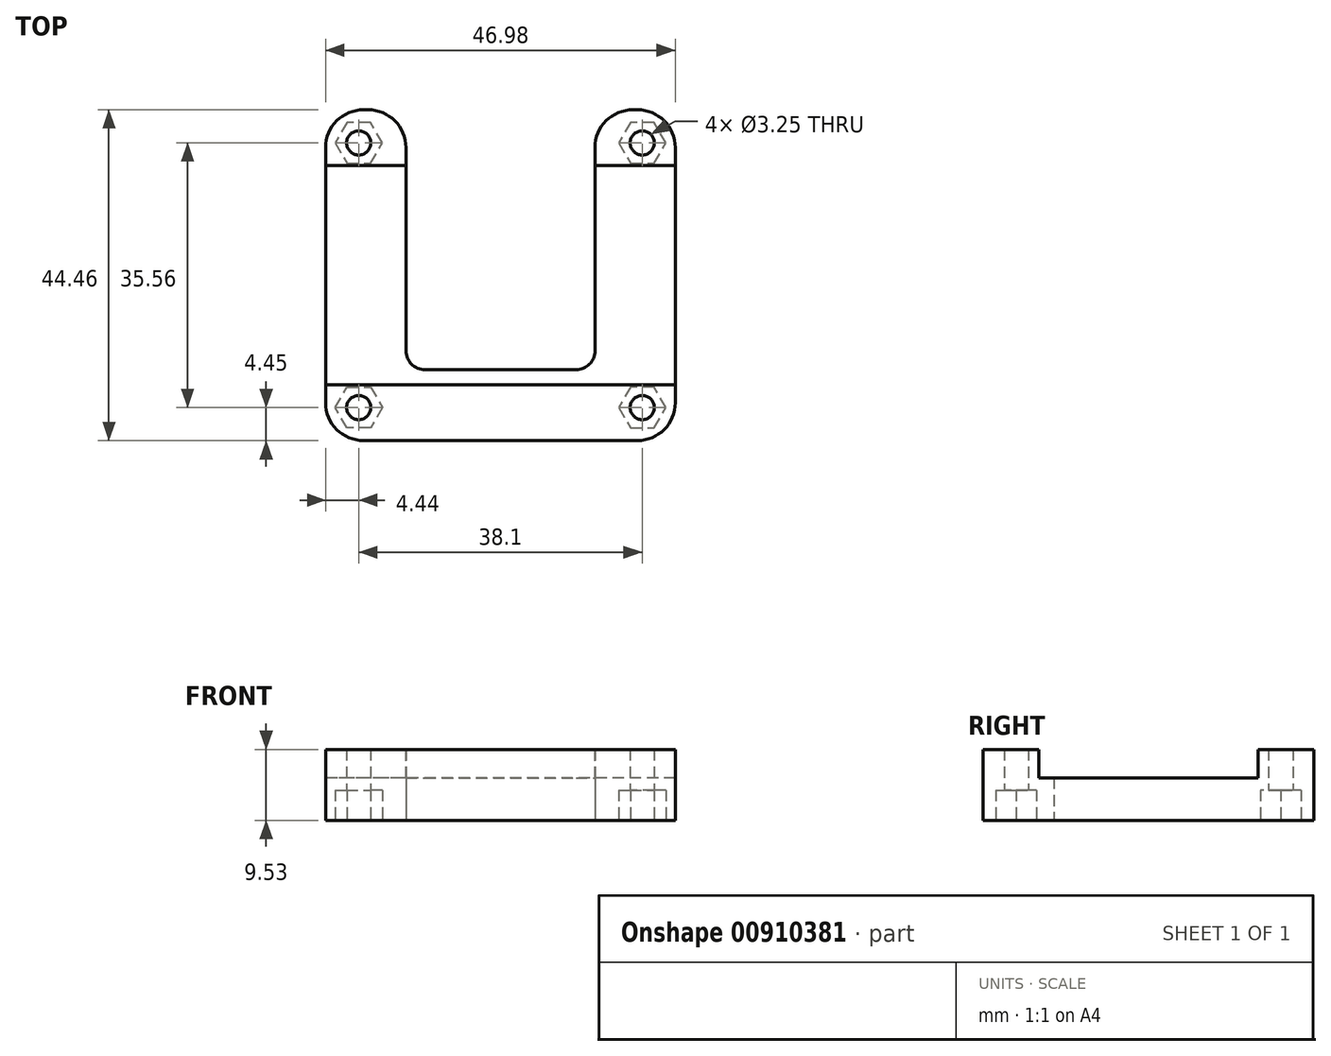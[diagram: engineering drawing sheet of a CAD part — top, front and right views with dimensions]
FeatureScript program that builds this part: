
annotation { "Feature Type Name" : "Feature", "Feature Type Description" : "" }
export const myFeature = defineFeature(function(context is Context, id is Id, definition is map)
    precondition{}
    {
        {
            var Q0;
            Q0=qCreatedBy(makeId("Top.planeOp"),FACE);
            var sketch = newSketch(context, id + "F0", { "sketchPlane" : qUnion([Q0])});
            skLineSegment(sketch, "E0.bottom", {"start": v(18.41, 22.23) * mm, "end": v(17.78, 22.23) * mm});
            skLineSegment(sketch, "E0.top", {"start": v(18.41, -22.23) * mm, "end": v(-18.42, -22.22) * mm});
            skLineSegment(sketch, "E0.left", {"start": v(23.5, 17.14) * mm, "end": v(23.5, -17.15) * mm});
            skLineSegment(sketch, "E0.right", {"start": v(-23.5, 17.14) * mm, "end": v(-23.5, -17.14) * mm});
            skPoint(sketch, "E0.middle", {"position": v(0, 0) * mm});
            skLineSegment(sketch, "E1.bottom", {"start": v(19.05, 17.78) * mm, "end": v(-19.05, 17.78) * mm, "construction": true});
            skLineSegment(sketch, "E1.top", {"start": v(19.05, -17.78) * mm, "end": v(-19.05, -17.78) * mm, "construction": true});
            skLineSegment(sketch, "E1.left", {"start": v(19.05, 17.78) * mm, "end": v(19.05, -17.78) * mm, "construction": true});
            skLineSegment(sketch, "E1.right", {"start": v(-19.05, 17.78) * mm, "end": v(-19.05, -17.78) * mm, "construction": true});
            skLineSegment(sketch, "E2", {"start": v(-12.7, 17.15) * mm, "end": v(-12.7, -10.16) * mm});
            skLineSegment(sketch, "E3", {"start": v(12.7, 17.15) * mm, "end": v(12.7, -10.16) * mm});
            skLineSegment(sketch, "E4.trimOffspring", {"start": v(-17.78, 22.23) * mm, "end": v(-18.41, 22.23) * mm});
            skPoint(sketch, "E5.visualSharp", {"position": v(-23.5, 22.23) * mm});
            skArc(sketch, "E5.filletArc", {"start": v(-18.41, 22.23) * mm, "mid": v(-22, 20.74) * mm, "end": v(-23.5, 17.14) * mm});
            skPoint(sketch, "E6.visualSharp", {"position": v(-12.7, 22.23) * mm});
            skArc(sketch, "E6.filletArc", {"start": v(-12.7, 17.15) * mm, "mid": v(-14.19, 20.74) * mm, "end": v(-17.78, 22.23) * mm});
            skPoint(sketch, "E7.visualSharp", {"position": v(12.7, 22.23) * mm});
            skArc(sketch, "E7.filletArc", {"start": v(17.78, 22.23) * mm, "mid": v(14.19, 20.74) * mm, "end": v(12.7, 17.15) * mm});
            skPoint(sketch, "E8.visualSharp", {"position": v(23.5, 22.22) * mm});
            skArc(sketch, "E8.filletArc", {"start": v(23.5, 17.14) * mm, "mid": v(22, 20.74) * mm, "end": v(18.41, 22.22) * mm});
            skPoint(sketch, "E9.visualSharp", {"position": v(23.5, -22.23) * mm});
            skArc(sketch, "E9.filletArc", {"start": v(18.41, -22.23) * mm, "mid": v(22, -20.74) * mm, "end": v(23.5, -17.15) * mm});
            skPoint(sketch, "E10.visualSharp", {"position": v(-23.5, -22.23) * mm});
            skArc(sketch, "E10.filletArc", {"start": v(-23.5, -17.14) * mm, "mid": v(-22, -20.74) * mm, "end": v(-18.42, -22.22) * mm});
            skCircle(sketch, "E11", {"center": v(-19.05, 17.78) * mm, "radius": 1.63 * mm});
            skCircle(sketch, "E12", {"center": v(19.05, 17.78) * mm, "radius": 1.63 * mm});
            skCircle(sketch, "E13", {"center": v(19.05, -17.78) * mm, "radius": 1.63 * mm});
            skCircle(sketch, "E14", {"center": v(-19.05, -17.78) * mm, "radius": 1.63 * mm});
            skLineSegment(sketch, "E15", {"start": v(-10.16, -12.7) * mm, "end": v(10.16, -12.7) * mm});
            skPoint(sketch, "E16.visualSharp", {"position": v(12.7, -12.7) * mm});
            skArc(sketch, "E16.filletArc", {"start": v(10.16, -12.7) * mm, "mid": v(11.96, -11.96) * mm, "end": v(12.7, -10.16) * mm});
            skPoint(sketch, "E17.visualSharp", {"position": v(-12.7, -12.7) * mm});
            skArc(sketch, "E17.filletArc", {"start": v(-12.7, -10.16) * mm, "mid": v(-11.96, -11.96) * mm, "end": v(-10.16, -12.7) * mm});
            skSolve(sketch);
        }
        {
            var Q0;
            Q0 = qSketchRegion(id + "F0", true);
            extrude(context, id + "F1", {"entities" : qUnion([Q0]), "depth" : 9.52 * mm, "offsetDistance" : 25.4 * mm});
        }
        {
            var Q0;
            Q0=makeQuery(id+"F1.opExtrude","CAP_FACE",FACE,{"disambiguationData":[OSD([sQuery(id+"F0.wireOp",EDGE,"E0.bottom"),sQuery(id+"F0.wireOp",EDGE,"E0.top"),sQuery(id+"F0.wireOp",EDGE,"E0.left"),sQuery(id+"F0.wireOp",EDGE,"E0.right"),sQuery(id+"F0.wireOp",EDGE,"E2"),sQuery(id+"F0.wireOp",EDGE,"E3"),sQuery(id+"F0.wireOp",EDGE,"1OHRI4IR-vGyN-WuqW-zxwV-OXcraFwO1tQ8"),sQuery(id+"F0.wireOp",EDGE,"E4.trimOffspring"),sQuery(id+"F0.wireOp",EDGE,"E5.filletArc"),sQuery(id+"F0.wireOp",EDGE,"E6.filletArc"),sQuery(id+"F0.wireOp",EDGE,"E7.filletArc"),sQuery(id+"F0.wireOp",EDGE,"E8.filletArc"),sQuery(id+"F0.wireOp",EDGE,"E9.filletArc"),sQuery(id+"F0.wireOp",EDGE,"E10.filletArc")])],"isStart":false});
            var sketch = newSketch(context, id + "F2", { "sketchPlane" : qUnion([Q0])});
            skLineSegment(sketch, "E18.bottom", {"start": v(23.5, 14.73) * mm, "end": v(-23.5, 14.73) * mm});
            skLineSegment(sketch, "E18.top", {"start": v(23.5, -14.73) * mm, "end": v(-23.5, -14.73) * mm});
            skLineSegment(sketch, "E18.left", {"start": v(23.5, 14.73) * mm, "end": v(23.5, -14.73) * mm});
            skLineSegment(sketch, "E18.right", {"start": v(-23.5, 14.73) * mm, "end": v(-23.5, -14.73) * mm});
            skPoint(sketch, "E18.middle", {"position": v(0, 0) * mm});
            skSolve(sketch);
        }
        {
            var Q0;
            Q0 = qSketchRegion(id + "F2", true);
            extrude(context, id + "F3", {"entities" : qUnion([Q0]), "operationType" : NewBodyOperationType.REMOVE, "oppositeDirection" : true, "depth" : 3.8 * mm, "offsetDistance" : 25.4 * mm});
        }
        {
            var Q0;
            Q0=makeQuery(id+"F1.opExtrude","CAP_FACE",FACE,{"disambiguationData":[OSD([sQuery(id+"F0.wireOp",EDGE,"E0.bottom"),sQuery(id+"F0.wireOp",EDGE,"E0.top"),sQuery(id+"F0.wireOp",EDGE,"E0.left"),sQuery(id+"F0.wireOp",EDGE,"E0.right"),sQuery(id+"F0.wireOp",EDGE,"E2"),sQuery(id+"F0.wireOp",EDGE,"E3"),sQuery(id+"F0.wireOp",EDGE,"1OHRI4IR-vGyN-WuqW-zxwV-OXcraFwO1tQ8"),sQuery(id+"F0.wireOp",EDGE,"E4.trimOffspring"),sQuery(id+"F0.wireOp",EDGE,"E5.filletArc"),sQuery(id+"F0.wireOp",EDGE,"E6.filletArc"),sQuery(id+"F0.wireOp",EDGE,"E7.filletArc"),sQuery(id+"F0.wireOp",EDGE,"E8.filletArc"),sQuery(id+"F0.wireOp",EDGE,"E9.filletArc"),sQuery(id+"F0.wireOp",EDGE,"E10.filletArc"),sQuery(id+"F0.wireOp",EDGE,"E11"),sQuery(id+"F0.wireOp",EDGE,"E12"),sQuery(id+"F0.wireOp",EDGE,"E13"),sQuery(id+"F0.wireOp",EDGE,"E14")])],"isStart":true});
            var sketch = newSketch(context, id + "F4", { "sketchPlane" : qUnion([Q0])});
            skCircle(sketch, "E19.cCircle", {"center": v(19.05, -17.78) * mm, "radius": 2.74 * mm, "construction": true});
            skLineSegment(sketch, "E19.0", {"start": v(15.88, -17.78) * mm, "end": v(17.47, -15.04) * mm});
            skLineSegment(sketch, "E19.1", {"start": v(17.47, -15.04) * mm, "end": v(20.63, -15.04) * mm});
            skLineSegment(sketch, "E19.2", {"start": v(20.63, -15.04) * mm, "end": v(22.22, -17.78) * mm});
            skLineSegment(sketch, "E19.3", {"start": v(22.22, -17.78) * mm, "end": v(20.63, -20.52) * mm});
            skLineSegment(sketch, "E19.4", {"start": v(20.63, -20.52) * mm, "end": v(17.47, -20.52) * mm});
            skLineSegment(sketch, "E19.5", {"start": v(17.47, -20.52) * mm, "end": v(15.88, -17.78) * mm});
            skPoint(sketch, "E19.0.midPoint", {"position": v(16.67, -16.4) * mm});
            skCircle(sketch, "E20.cCircle", {"center": v(-19.05, -17.78) * mm, "radius": 2.74 * mm, "construction": true});
            skLineSegment(sketch, "E20.0", {"start": v(-20.63, -15.04) * mm, "end": v(-17.47, -15.04) * mm});
            skLineSegment(sketch, "E20.1", {"start": v(-17.47, -15.04) * mm, "end": v(-15.88, -17.78) * mm});
            skLineSegment(sketch, "E20.2", {"start": v(-15.88, -17.78) * mm, "end": v(-17.47, -20.52) * mm});
            skLineSegment(sketch, "E20.3", {"start": v(-17.47, -20.52) * mm, "end": v(-20.63, -20.52) * mm});
            skLineSegment(sketch, "E20.4", {"start": v(-20.63, -20.52) * mm, "end": v(-22.22, -17.78) * mm});
            skLineSegment(sketch, "E20.5", {"start": v(-22.22, -17.78) * mm, "end": v(-20.63, -15.04) * mm});
            skPoint(sketch, "E20.0.midPoint", {"position": v(-19.05, -15.04) * mm});
            skCircle(sketch, "E21.cCircle", {"center": v(19.05, 17.78) * mm, "radius": 2.74 * mm, "construction": true});
            skLineSegment(sketch, "E21.0", {"start": v(17.47, 15.04) * mm, "end": v(15.88, 17.78) * mm});
            skLineSegment(sketch, "E21.1", {"start": v(15.88, 17.78) * mm, "end": v(17.47, 20.52) * mm});
            skLineSegment(sketch, "E21.2", {"start": v(17.47, 20.52) * mm, "end": v(20.63, 20.52) * mm});
            skLineSegment(sketch, "E21.3", {"start": v(20.63, 20.52) * mm, "end": v(22.22, 17.78) * mm});
            skLineSegment(sketch, "E21.4", {"start": v(22.22, 17.78) * mm, "end": v(20.63, 15.04) * mm});
            skLineSegment(sketch, "E21.5", {"start": v(20.63, 15.04) * mm, "end": v(17.47, 15.04) * mm});
            skPoint(sketch, "E21.0.midPoint", {"position": v(16.67, 16.4) * mm});
            skCircle(sketch, "E22.cCircle", {"center": v(-19.05, 17.78) * mm, "radius": 2.74 * mm, "construction": true});
            skLineSegment(sketch, "E22.0", {"start": v(-20.63, 15.04) * mm, "end": v(-17.47, 15.04) * mm});
            skLineSegment(sketch, "E22.1", {"start": v(-22.22, 17.78) * mm, "end": v(-20.63, 15.04) * mm});
            skLineSegment(sketch, "E22.2", {"start": v(-20.63, 20.52) * mm, "end": v(-22.22, 17.78) * mm});
            skLineSegment(sketch, "E22.3", {"start": v(-17.47, 20.52) * mm, "end": v(-20.63, 20.52) * mm});
            skLineSegment(sketch, "E22.4", {"start": v(-15.88, 17.78) * mm, "end": v(-17.47, 20.52) * mm});
            skLineSegment(sketch, "E22.5", {"start": v(-17.47, 15.04) * mm, "end": v(-15.88, 17.78) * mm});
            skPoint(sketch, "E22.0.midPoint", {"position": v(-19.05, 15.04) * mm});
            skSolve(sketch);
        }
        {
            var Q0;
            Q0 = qSketchRegion(id + "F4", true);
            extrude(context, id + "F5", {"entities" : qUnion([Q0]), "operationType" : NewBodyOperationType.REMOVE, "oppositeDirection" : true, "depth" : 4.06 * mm, "offsetDistance" : 25.4 * mm});
        }
    });
